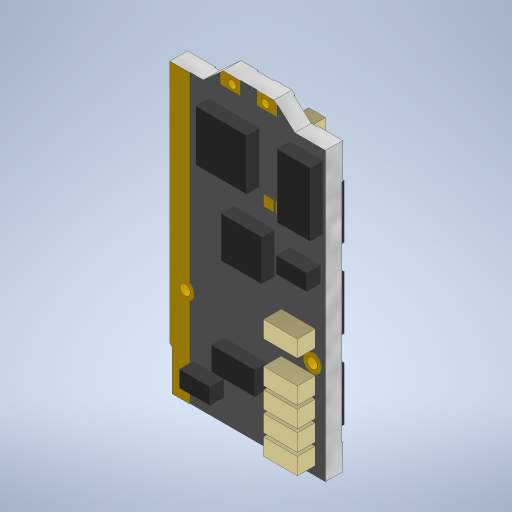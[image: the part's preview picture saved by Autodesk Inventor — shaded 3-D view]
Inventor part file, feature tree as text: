
AUTODESK INVENTOR PART (.ipt)
format: ipt  version: 2023.1 (Build 271208000, 208)  size: 608,768 bytes
history: native  units: in
note: dims shown in document units (in); Inventor stores cm internally (conversion verified against a paired STEP export)
features: extrude x13, sketch x10, chamfer x1
ambient origin geometry x8: Origin, YZ Plane, XZ Plane, XY Plane, X Axis, Y Axis, Z Axis, Center Point
bodies: Solid1 (feature_tree)
feature tree (24):
  extrude  "Extrusion1"  Depth=1.1811in
  sketch  "Sketch3"  dims[d2=0.063in d3=0.0in d4=1.1102in]
  extrude  "Extrusion2"  Depth=1.1102in
  extrude  "Extrusion3"  Depth=0.3543in
  extrude  "Extrusion4"  Depth=0.0512in
  extrude  "Extrusion5"  Depth=0.0669in
  extrude  "Extrusion6"  Depth=0.0492in
  extrude  "Extrusion7"  Depth=0.374in
  extrude  "Extrusion8"  Depth=0.0394in
  chamfer  "Chamfer1"  Distance=0.0079in
  extrude  "Extrusion9"  Depth=0.2657in
  extrude  "Extrusion10"  Depth=0.1516in
  extrude  "Extrusion11"  Depth=0.0295in
  extrude  "Extrusion12"  Depth=0.128in
  extrude  "Extrusion13"  Depth=0.0276in
  sketch  "Sketch1"  dims[d0=0.5906in d1=1.1811in]
  sketch  "Sketch4"  dims[d5=0.1969in d6=0.3543in]
  sketch  "Sketch5"  dims[d8=0.0787in d9=0.0512in]
  sketch  "Sketch6"  dims[d10=0.2205in d11=0.0669in]
  sketch  "Sketch7"  dims[d12=0.0394in d13=0.0492in]
  sketch  "Sketch8"  dims[d14=0.0709in d15=0.374in]
  sketch  "Sketch9"  dims[d16=0.0394in d17=0.0394in]
  sketch  "Sketch10"  dims[d18=0.0394in]
  sketch  "Sketch11"  dims[d19=0.0394in d20=0.0079in d21=0.2657in d22=0.1516in d23=0.0295in d24=0.128in d25=0.0276in d26=0.002in d27=0.0in d28=0.0098in d29=0.9449in d30=45.0deg d31=0.002in d32=0.063in d33=0.0in d34=0.0in d35=0.002in d36=0.0in d37=0.0669in d38=0.0in d39=0.0984in d40=0.1378in d41=0.0984in d42=0.1378in d43=0.1339in d44=0.0984in d45=0.1378in d46=0.0984in d47=0.1378in d48=0.0984in d49=0.0787in d50=0.0039in d51=0.0in d52=0.2067in d53=0.2264in d54=0.0394in d55=0.0394in d63=1.1811in d65=0.3051in d66=0.7874in d68=0.2657in d71=0.1339in d72=0.1339in d73=0.25in d74=0.0197in d75=0.0492in d76=0.0in d77=0.1083in d78=0.0039in d79=0.0in d80=0.0039in d81=0.0787in d82=45.0deg d83=0.065in d84=0.1319in d85=0.1969in d86=0.1319in d87=0.065in d88=0.2657in d89=0.0197in d90=0.1319in d91=0.065in d92=0.0197in d93=0.0689in d94=0.0in d95=0.1969in d96=0.1969in d97=0.0531in d98=0.2559in d99=0.1575in d100=0.1575in d101=0.1969in d102=0.3642in d103=0.128in d104=0.2461in d105=0.0394in d106=0.0098in d107=0.0492in d108=0.0in d109=0.1319in d110=0.065in d111=0.0344in d112=0.0394in d113=1.5748in d115=0.0787in d116=0.3937in d118=0.3937in d120=0.1319in d121=0.065in d122=0.0925in d123=0.0689in d124=0.0in d125=0.1181in d126=0.063in d127=0.0197in d128=0.3937in d129=0.0531in d130=0.0in d131=0.1181in d132=0.063in d133=0.1476in d134=0.5118in d135=0.1673in d136=0.0906in d137=0.3937in d138=0.2854in d139=0.0472in d140=0.0in]
